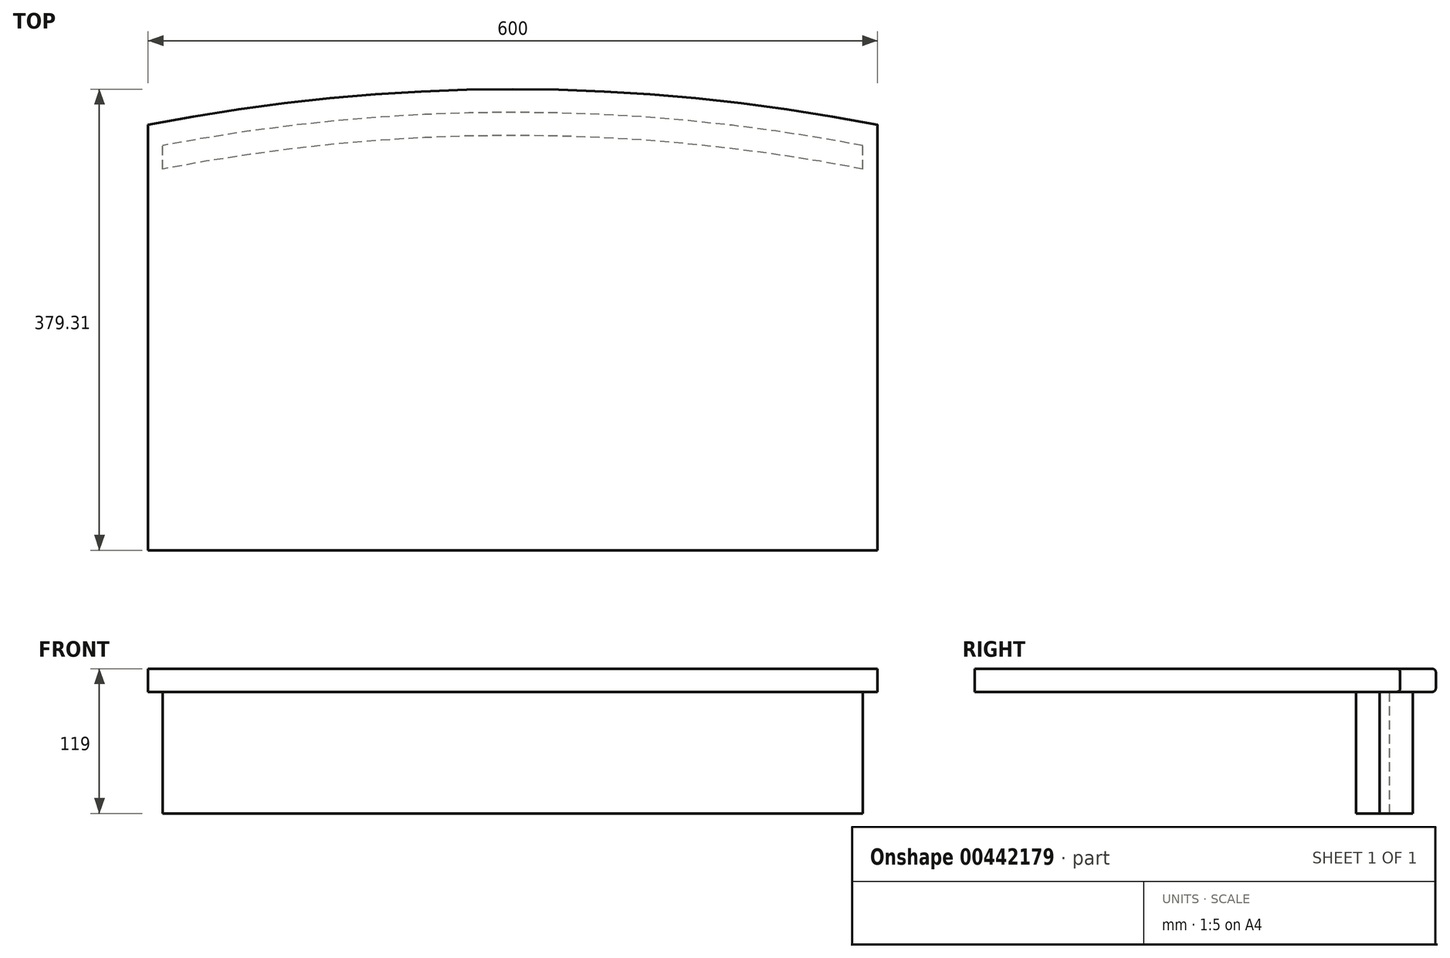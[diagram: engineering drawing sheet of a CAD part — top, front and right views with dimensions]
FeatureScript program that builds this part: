
annotation { "Feature Type Name" : "Feature", "Feature Type Description" : "" }
export const myFeature = defineFeature(function(context is Context, id is Id, definition is map)
    precondition{}
    {
        {
            var Q0;
            Q0=qCreatedBy(makeId("Top.planeOp"),FACE);
            var sketch = newSketch(context, id + "F0", { "sketchPlane" : qUnion([Q0])});
            skLineSegment(sketch, "E0.bottom", {"start": v(300, -175) * mm, "end": v(-300, -175) * mm});
            skLineSegment(sketch, "E0.left", {"start": v(300, -175) * mm, "end": v(300, 175) * mm});
            skLineSegment(sketch, "E0.right", {"start": v(-300, -175) * mm, "end": v(-300, 175) * mm});
            skPoint(sketch, "E0.middle", {"position": v(0, 0) * mm});
            skArc(sketch, "E1", {"start": v(-300, 175) * mm, "mid": v(0, 204.3) * mm, "end": v(300, 175) * mm});
            skPoint(sketch, "E2", {"position": v(200, 191.35) * mm});
            skPoint(sketch, "E3", {"position": v(100, 201.08) * mm});
            skSolve(sketch);
        }
        {
            var Q0;
            Q0=qSketchRegion(id+"F0",true);
            extrude(context, id + "F1", {"entities" : qUnion([Q0]), "depth" : 19 * mm});
        }
        {
            var Q0;
            Q0=makeQuery(id+"F1.opExtrude","CAP_FACE",FACE,{"disambiguationData":[OSD([sQuery(id+"F0.wireOp",EDGE,"E0.bottom"),sQuery(id+"F0.wireOp",EDGE,"E0.left"),sQuery(id+"F0.wireOp",EDGE,"E0.right"),sQuery(id+"F0.wireOp",EDGE,"E1")])],"isStart":true});
            var sketch = newSketch(context, id + "F2", { "sketchPlane" : qUnion([Q0])});
            skArc(sketch, "E4.0", {"start": v(-288, -157.98) * mm, "mid": v(0, -185.3) * mm, "end": v(288, -157.98) * mm});
            skArc(sketch, "E5.0", {"start": v(-288, -138.63) * mm, "mid": v(0, -166.3) * mm, "end": v(288, -138.63) * mm});
            skLineSegment(sketch, "E6", {"start": v(288, -138.63) * mm, "end": v(288, -157.98) * mm});
            skLineSegment(sketch, "E7", {"start": v(-288, -138.63) * mm, "end": v(-288, -157.98) * mm});
            skSolve(sketch);
        }
        {
            var Q0;
            Q0 = qSketchRegion(id + "F2", true);
            extrude(context, id + "F3", {"entities" : qUnion([Q0]), "operationType" : NewBodyOperationType.ADD, "depth" : 100 * mm});
        }
        {
            var Q0;
            Q0=makeQuery(id+"F1.opExtrude","CAP_EDGE",EDGE,{"disambiguationData":[OSD([sQuery(id+"F0.wireOp",EDGE,"E1")])],"isStart":false});
            var Q1;
            Q1=makeQuery(id+"F1.opExtrude","CAP_EDGE",EDGE,{"disambiguationData":[OSD([sQuery(id+"F0.wireOp",EDGE,"E1")])],"isStart":true});
            fillet(context, id + "F4", {"entities" : qUnion([Q0, Q1]), "radius" : 3 * mm, "tangentPropagation" : true, "allowEdgeOverflow" : false});
        }
    });
